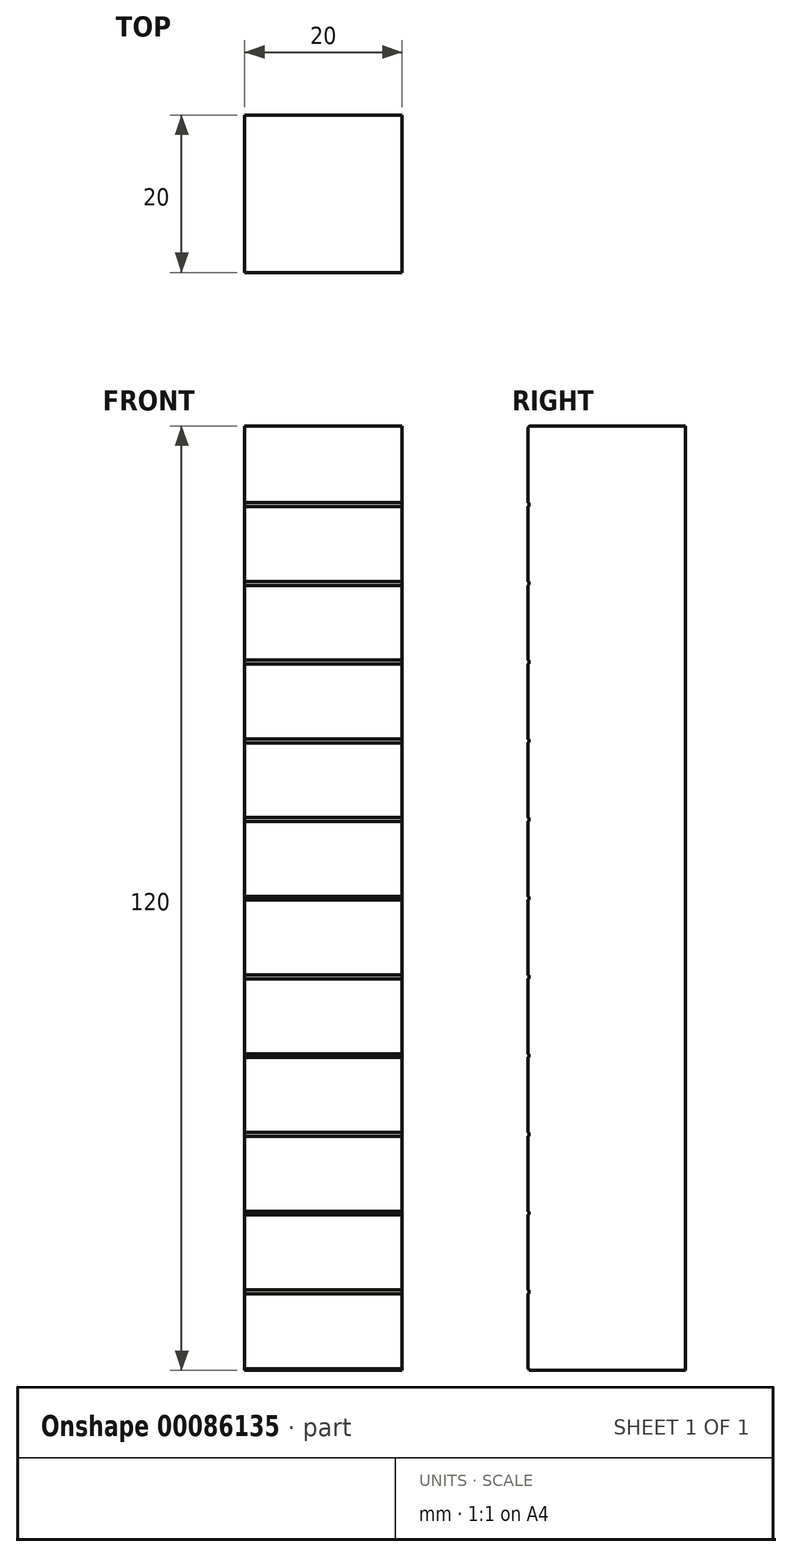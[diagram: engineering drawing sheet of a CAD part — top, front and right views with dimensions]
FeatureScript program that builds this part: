
annotation { "Feature Type Name" : "Feature", "Feature Type Description" : "" }
export const myFeature = defineFeature(function(context is Context, id is Id, definition is map)
    precondition{}
    {
        {
            var Q0;
            Q0=qCreatedBy(makeId("Top.planeOp"),FACE);
            var sketch = newSketch(context, id + "F0", { "sketchPlane" : qUnion([Q0])});
            skLineSegment(sketch, "E0.bottom", {"start": v(10, -10) * mm, "end": v(-10, -10) * mm});
            skLineSegment(sketch, "E0.top", {"start": v(10, 10) * mm, "end": v(-10, 10) * mm});
            skLineSegment(sketch, "E0.left", {"start": v(10, -10) * mm, "end": v(10, 10) * mm});
            skLineSegment(sketch, "E0.right", {"start": v(-10, -10) * mm, "end": v(-10, 10) * mm});
            skPoint(sketch, "E0.middle", {"position": v(0, 0) * mm});
            skSolve(sketch);
        }
        {
            var Q0;
            Q0 = qSketchRegion(id + "F0", true);
            extrude(context, id + "F1", {"entities" : qUnion([Q0]), "depth" : 120 * mm});
        }
        {
            var Q0;
            Q0=makeQuery(id+"F1.opExtrude","SWEPT_FACE",FACE,{"disambiguationData":[OSD([sQuery(id+"F0.wireOp",EDGE,"E0.bottom")])]});
            var sketch = newSketch(context, id + "F2", { "sketchPlane" : qUnion([Q0])});
            skLineSegment(sketch, "E1", {"start": v(-10, 0) * mm, "end": v(10, 0) * mm});
            skLineSegment(sketch, "E2.0.1.0", {"start": v(-10, 10) * mm, "end": v(10, 10) * mm});
            skLineSegment(sketch, "E2.0.2.0", {"start": v(-10, 20) * mm, "end": v(10, 20) * mm});
            skLineSegment(sketch, "E2.0.3.0", {"start": v(-10, 30) * mm, "end": v(10, 30) * mm});
            skLineSegment(sketch, "E2.0.4.0", {"start": v(-10, 40) * mm, "end": v(10, 40) * mm});
            skLineSegment(sketch, "E2.0.5.0", {"start": v(-10, 50) * mm, "end": v(10, 50) * mm});
            skLineSegment(sketch, "E2.0.6.0", {"start": v(-10, 60) * mm, "end": v(10, 60) * mm});
            skLineSegment(sketch, "E2.0.7.0", {"start": v(-10, 70) * mm, "end": v(10, 70) * mm});
            skLineSegment(sketch, "E2.0.8.0", {"start": v(-10, 80) * mm, "end": v(10, 80) * mm});
            skLineSegment(sketch, "E2.0.9.0", {"start": v(-10, 90) * mm, "end": v(10, 90) * mm});
            skLineSegment(sketch, "E2.0.10.0", {"start": v(-10, 100) * mm, "end": v(10, 100) * mm});
            skLineSegment(sketch, "E2.0.11.0", {"start": v(-10, 110) * mm, "end": v(10, 110) * mm});
            skLineSegment(sketch, "E2.direction1", {"start": v(-10, 0) * mm, "end": v(15, 0) * mm, "construction": true});
            skLineSegment(sketch, "E2.direction2", {"start": v(-10, 0) * mm, "end": v(-10, 10) * mm, "construction": true});
            skArc(sketch, "E3.0.startCap", {"start": v(-10, 109.75) * mm, "mid": v(-10.25, 110) * mm, "end": v(-10, 110.25) * mm});
            skArc(sketch, "E3.0.endCap", {"start": v(10, 110.25) * mm, "mid": v(10.25, 110) * mm, "end": v(10, 109.75) * mm});
            skLineSegment(sketch, "E3.0.left", {"start": v(-10, 110.25) * mm, "end": v(10, 110.25) * mm});
            skLineSegment(sketch, "E3.0.right", {"start": v(-10, 109.75) * mm, "end": v(10, 109.75) * mm});
            skArc(sketch, "E3.1.startCap", {"start": v(-10, -0.25) * mm, "mid": v(-10.25, 0) * mm, "end": v(-10, 0.25) * mm});
            skArc(sketch, "E3.1.endCap", {"start": v(15, 0.25) * mm, "mid": v(15.25, 0) * mm, "end": v(15, -0.25) * mm});
            skLineSegment(sketch, "E3.1.left", {"start": v(-10, 0.25) * mm, "end": v(15, 0.25) * mm});
            skLineSegment(sketch, "E3.1.right", {"start": v(-10, -0.25) * mm, "end": v(15, -0.25) * mm});
            skArc(sketch, "E3.2.startCap", {"start": v(-10, 9.75) * mm, "mid": v(-10.25, 10) * mm, "end": v(-10, 10.25) * mm});
            skArc(sketch, "E3.2.endCap", {"start": v(10, 10.25) * mm, "mid": v(10.25, 10) * mm, "end": v(10, 9.75) * mm});
            skLineSegment(sketch, "E3.2.left", {"start": v(-10, 10.25) * mm, "end": v(10, 10.25) * mm});
            skLineSegment(sketch, "E3.2.right", {"start": v(-10, 9.75) * mm, "end": v(10, 9.75) * mm});
            skArc(sketch, "E3.3.startCap", {"start": v(-10, 19.75) * mm, "mid": v(-10.25, 20) * mm, "end": v(-10, 20.25) * mm});
            skArc(sketch, "E3.3.endCap", {"start": v(10, 20.25) * mm, "mid": v(10.25, 20) * mm, "end": v(10, 19.75) * mm});
            skLineSegment(sketch, "E3.3.left", {"start": v(-10, 20.25) * mm, "end": v(10, 20.25) * mm});
            skLineSegment(sketch, "E3.3.right", {"start": v(-10, 19.75) * mm, "end": v(10, 19.75) * mm});
            skArc(sketch, "E3.4.startCap", {"start": v(-10, 29.75) * mm, "mid": v(-10.25, 30) * mm, "end": v(-10, 30.25) * mm});
            skArc(sketch, "E3.4.endCap", {"start": v(10, 30.25) * mm, "mid": v(10.25, 30) * mm, "end": v(10, 29.75) * mm});
            skLineSegment(sketch, "E3.4.left", {"start": v(-10, 30.25) * mm, "end": v(10, 30.25) * mm});
            skLineSegment(sketch, "E3.4.right", {"start": v(-10, 29.75) * mm, "end": v(10, 29.75) * mm});
            skArc(sketch, "E3.5.startCap", {"start": v(-10, 39.75) * mm, "mid": v(-10.25, 40) * mm, "end": v(-10, 40.25) * mm});
            skArc(sketch, "E3.5.endCap", {"start": v(10, 40.25) * mm, "mid": v(10.25, 40) * mm, "end": v(10, 39.75) * mm});
            skLineSegment(sketch, "E3.5.left", {"start": v(-10, 40.25) * mm, "end": v(10, 40.25) * mm});
            skLineSegment(sketch, "E3.5.right", {"start": v(-10, 39.75) * mm, "end": v(10, 39.75) * mm});
            skArc(sketch, "E3.6.startCap", {"start": v(-10, 49.75) * mm, "mid": v(-10.25, 50) * mm, "end": v(-10, 50.25) * mm});
            skArc(sketch, "E3.6.endCap", {"start": v(10, 50.25) * mm, "mid": v(10.25, 50) * mm, "end": v(10, 49.75) * mm});
            skLineSegment(sketch, "E3.6.left", {"start": v(-10, 50.25) * mm, "end": v(10, 50.25) * mm});
            skLineSegment(sketch, "E3.6.right", {"start": v(-10, 49.75) * mm, "end": v(10, 49.75) * mm});
            skArc(sketch, "E3.7.startCap", {"start": v(-10, 59.75) * mm, "mid": v(-10.25, 60) * mm, "end": v(-10, 60.25) * mm});
            skArc(sketch, "E3.7.endCap", {"start": v(10, 60.25) * mm, "mid": v(10.25, 60) * mm, "end": v(10, 59.75) * mm});
            skLineSegment(sketch, "E3.7.left", {"start": v(-10, 60.25) * mm, "end": v(10, 60.25) * mm});
            skLineSegment(sketch, "E3.7.right", {"start": v(-10, 59.75) * mm, "end": v(10, 59.75) * mm});
            skArc(sketch, "E3.8.startCap", {"start": v(-10, 69.75) * mm, "mid": v(-10.25, 70) * mm, "end": v(-10, 70.25) * mm});
            skArc(sketch, "E3.8.endCap", {"start": v(10, 70.25) * mm, "mid": v(10.25, 70) * mm, "end": v(10, 69.75) * mm});
            skLineSegment(sketch, "E3.8.left", {"start": v(-10, 70.25) * mm, "end": v(10, 70.25) * mm});
            skLineSegment(sketch, "E3.8.right", {"start": v(-10, 69.75) * mm, "end": v(10, 69.75) * mm});
            skArc(sketch, "E3.9.startCap", {"start": v(-10, 79.75) * mm, "mid": v(-10.25, 80) * mm, "end": v(-10, 80.25) * mm});
            skArc(sketch, "E3.9.endCap", {"start": v(10, 80.25) * mm, "mid": v(10.25, 80) * mm, "end": v(10, 79.75) * mm});
            skLineSegment(sketch, "E3.9.left", {"start": v(-10, 80.25) * mm, "end": v(10, 80.25) * mm});
            skLineSegment(sketch, "E3.9.right", {"start": v(-10, 79.75) * mm, "end": v(10, 79.75) * mm});
            skArc(sketch, "E3.10.startCap", {"start": v(-10, 89.75) * mm, "mid": v(-10.25, 90) * mm, "end": v(-10, 90.25) * mm});
            skArc(sketch, "E3.10.endCap", {"start": v(10, 90.25) * mm, "mid": v(10.25, 90) * mm, "end": v(10, 89.75) * mm});
            skLineSegment(sketch, "E3.10.left", {"start": v(-10, 90.25) * mm, "end": v(10, 90.25) * mm});
            skLineSegment(sketch, "E3.10.right", {"start": v(-10, 89.75) * mm, "end": v(10, 89.75) * mm});
            skArc(sketch, "E3.11.startCap", {"start": v(-10, 99.75) * mm, "mid": v(-10.25, 100) * mm, "end": v(-10, 100.25) * mm});
            skArc(sketch, "E3.11.endCap", {"start": v(10, 100.25) * mm, "mid": v(10.25, 100) * mm, "end": v(10, 99.75) * mm});
            skLineSegment(sketch, "E3.11.left", {"start": v(-10, 100.25) * mm, "end": v(10, 100.25) * mm});
            skLineSegment(sketch, "E3.11.right", {"start": v(-10, 99.75) * mm, "end": v(10, 99.75) * mm});
            skSolve(sketch);
        }
        {
            var Q0;
            Q0 = qSketchRegion(id + "F2", true);
            extrude(context, id + "F3", {"entities" : qUnion([Q0]), "operationType" : NewBodyOperationType.REMOVE, "oppositeDirection" : true, "depth" : .125 * mm});
        }
        {
            var Q0;
            Q0=makeQuery(id+"F3.boolean.opBoolean","COPY",EDGE,{"derivedFrom":makeQuery(id+"F3.opExtrude","CAP_EDGE",EDGE,{"disambiguationData":[OSD([sQuery(id+"F2.wireOp",EDGE,"E3.7.right")])],"isStart":false})});
            var Q1;
            Q1=makeQuery(id+"F3.boolean.opBoolean","COPY",EDGE,{"derivedFrom":makeQuery(id+"F3.opExtrude","CAP_EDGE",EDGE,{"disambiguationData":[OSD([sQuery(id+"F2.wireOp",EDGE,"E3.7.left")])],"isStart":false})});
            var Q2;
            Q2=makeQuery(id+"F3.boolean.opBoolean","COPY",EDGE,{"derivedFrom":makeQuery(id+"F3.opExtrude","CAP_EDGE",EDGE,{"disambiguationData":[OSD([sQuery(id+"F2.wireOp",EDGE,"E3.1.left")])],"isStart":false})});
            var Q3;
            Q3=makeQuery(id+"F3.boolean.opBoolean","COPY",EDGE,{"derivedFrom":makeQuery(id+"F3.opExtrude","CAP_EDGE",EDGE,{"disambiguationData":[OSD([sQuery(id+"F2.wireOp",EDGE,"E3.2.right")])],"isStart":false})});
            var Q4;
            Q4=makeQuery(id+"F3.boolean.opBoolean","COPY",EDGE,{"derivedFrom":makeQuery(id+"F3.opExtrude","CAP_EDGE",EDGE,{"disambiguationData":[OSD([sQuery(id+"F2.wireOp",EDGE,"E3.2.left")])],"isStart":false})});
            var Q5;
            Q5=makeQuery(id+"F3.boolean.opBoolean","COPY",EDGE,{"derivedFrom":makeQuery(id+"F3.opExtrude","CAP_EDGE",EDGE,{"disambiguationData":[OSD([sQuery(id+"F2.wireOp",EDGE,"E3.3.left")])],"isStart":false})});
            var Q6;
            Q6=makeQuery(id+"F3.boolean.opBoolean","COPY",EDGE,{"derivedFrom":makeQuery(id+"F3.opExtrude","CAP_EDGE",EDGE,{"disambiguationData":[OSD([sQuery(id+"F2.wireOp",EDGE,"E3.3.right")])],"isStart":false})});
            var Q7;
            Q7=makeQuery(id+"F3.boolean.opBoolean","COPY",EDGE,{"derivedFrom":makeQuery(id+"F3.opExtrude","CAP_EDGE",EDGE,{"disambiguationData":[OSD([sQuery(id+"F2.wireOp",EDGE,"E3.4.right")])],"isStart":false})});
            var Q8;
            Q8=makeQuery(id+"F3.boolean.opBoolean","COPY",EDGE,{"derivedFrom":makeQuery(id+"F3.opExtrude","CAP_EDGE",EDGE,{"disambiguationData":[OSD([sQuery(id+"F2.wireOp",EDGE,"E3.4.left")])],"isStart":false})});
            var Q9;
            Q9=makeQuery(id+"F3.boolean.opBoolean","COPY",EDGE,{"derivedFrom":makeQuery(id+"F3.opExtrude","CAP_EDGE",EDGE,{"disambiguationData":[OSD([sQuery(id+"F2.wireOp",EDGE,"E3.5.left")])],"isStart":false})});
            var Q10;
            Q10=makeQuery(id+"F3.boolean.opBoolean","COPY",EDGE,{"derivedFrom":makeQuery(id+"F3.opExtrude","CAP_EDGE",EDGE,{"disambiguationData":[OSD([sQuery(id+"F2.wireOp",EDGE,"E3.5.right")])],"isStart":false})});
            var Q11;
            Q11=makeQuery(id+"F3.boolean.opBoolean","COPY",EDGE,{"derivedFrom":makeQuery(id+"F3.opExtrude","CAP_EDGE",EDGE,{"disambiguationData":[OSD([sQuery(id+"F2.wireOp",EDGE,"E3.6.right")])],"isStart":false})});
            var Q12;
            Q12=makeQuery(id+"F3.boolean.opBoolean","COPY",EDGE,{"derivedFrom":makeQuery(id+"F3.opExtrude","CAP_EDGE",EDGE,{"disambiguationData":[OSD([sQuery(id+"F2.wireOp",EDGE,"E3.6.left")])],"isStart":false})});
            var Q13;
            Q13=makeQuery(id+"F3.boolean.opBoolean","COPY",EDGE,{"derivedFrom":makeQuery(id+"F3.opExtrude","CAP_EDGE",EDGE,{"disambiguationData":[OSD([sQuery(id+"F2.wireOp",EDGE,"E3.8.left")])],"isStart":false})});
            var Q14;
            Q14=makeQuery(id+"F3.boolean.opBoolean","COPY",EDGE,{"derivedFrom":makeQuery(id+"F3.opExtrude","CAP_EDGE",EDGE,{"disambiguationData":[OSD([sQuery(id+"F2.wireOp",EDGE,"E3.8.right")])],"isStart":false})});
            var Q15;
            Q15=makeQuery(id+"F3.boolean.opBoolean","COPY",EDGE,{"derivedFrom":makeQuery(id+"F3.opExtrude","CAP_EDGE",EDGE,{"disambiguationData":[OSD([sQuery(id+"F2.wireOp",EDGE,"E3.9.right")])],"isStart":false})});
            var Q16;
            Q16=makeQuery(id+"F3.boolean.opBoolean","COPY",EDGE,{"derivedFrom":makeQuery(id+"F3.opExtrude","CAP_EDGE",EDGE,{"disambiguationData":[OSD([sQuery(id+"F2.wireOp",EDGE,"E3.9.left")])],"isStart":false})});
            var Q17;
            Q17=makeQuery(id+"F3.boolean.opBoolean","COPY",EDGE,{"derivedFrom":makeQuery(id+"F3.opExtrude","CAP_EDGE",EDGE,{"disambiguationData":[OSD([sQuery(id+"F2.wireOp",EDGE,"E3.10.left")])],"isStart":false})});
            var Q18;
            Q18=makeQuery(id+"F3.boolean.opBoolean","COPY",EDGE,{"derivedFrom":makeQuery(id+"F3.opExtrude","CAP_EDGE",EDGE,{"disambiguationData":[OSD([sQuery(id+"F2.wireOp",EDGE,"E3.10.right")])],"isStart":false})});
            var Q19;
            Q19=makeQuery(id+"F3.boolean.opBoolean","COPY",EDGE,{"derivedFrom":makeQuery(id+"F3.opExtrude","CAP_EDGE",EDGE,{"disambiguationData":[OSD([sQuery(id+"F2.wireOp",EDGE,"E3.11.left")])],"isStart":false})});
            var Q20;
            Q20=makeQuery(id+"F3.boolean.opBoolean","COPY",EDGE,{"derivedFrom":makeQuery(id+"F3.opExtrude","CAP_EDGE",EDGE,{"disambiguationData":[OSD([sQuery(id+"F2.wireOp",EDGE,"E3.11.right")])],"isStart":false})});
            var Q21;
            Q21=makeQuery(id+"F3.boolean.opBoolean","COPY",EDGE,{"derivedFrom":makeQuery(id+"F3.opExtrude","CAP_EDGE",EDGE,{"disambiguationData":[OSD([sQuery(id+"F2.wireOp",EDGE,"E3.0.right")])],"isStart":false})});
            var Q22;
            Q22=makeQuery(id+"F3.boolean.opBoolean","COPY",EDGE,{"derivedFrom":makeQuery(id+"F3.opExtrude","CAP_EDGE",EDGE,{"disambiguationData":[OSD([sQuery(id+"F2.wireOp",EDGE,"E3.0.left")])],"isStart":false})});
            var Q23;
            Q23=makeQuery(id+"F1.opExtrude","CAP_EDGE",EDGE,{"disambiguationData":[OSD([sQuery(id+"F0.wireOp",EDGE,"E0.bottom")])],"isStart":false});
            fillet(context, id + "F4", {"entities" : qUnion([Q0, Q1, Q2, Q3, Q4, Q5, Q6, Q7, Q8, Q9, Q10, Q11, Q12, Q13, Q14, Q15, Q16, Q17, Q18, Q19, Q20, Q21, Q22, Q23]), "radius" : .3125 * mm, "tangentPropagation" : true, "allowEdgeOverflow" : false});
        }
    });
